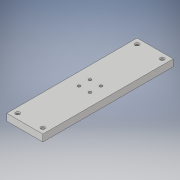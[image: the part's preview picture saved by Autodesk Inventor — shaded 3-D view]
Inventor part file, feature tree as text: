
AUTODESK INVENTOR PART (.ipt)
format: ipt  version: 2019.4 (Build 234330000, 330)  size: 123,904 bytes
history: native  units: in
note: dims shown in document units (in); Inventor stores cm internally (conversion verified against a paired STEP export)
features: sketch x3, hole x2, extrude x1
ambient origin geometry x8: Origin, YZ Plane, XZ Plane, XY Plane, X Axis, Y Axis, Z Axis, Center Point
bodies: Solid1 (feature_tree)
feature tree (6):
  extrude  "Extrusion1"  Depth=1.0354in
  hole  "Hole1"  [1 undecoded]
  hole  "Hole2"  [1 undecoded]
  sketch  "Sketch1"  dims[d0=3.7402in d1=1.0354in]
  sketch  "Sketch2"  dims[d2=0.1969in d3=0.0in d4=0.1181in]
  sketch  "Sketch3"  dims[d5=0.1575in d6=0.1575in d7=0.1575in d8=0.1575in d9=0.0787in d10=0.339in d11=0.119in d12=0.25in d13=0.5635in d14=0.617in d15=0.8108in d16=0.1181in d17=0.1575in d18=0.1575in d19=0.1575in d20=0.1575in d21=0.0787in d22=0.339in d23=0.119in d24=0.25in d25=0.5635in d26=0.617in d27=0.8108in]
note: 2 required parameter values undecoded (feature->parameter linkage not recoverable at this tier; creation-order binding heuristic only, values carry confidence <= 0.55)
